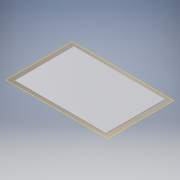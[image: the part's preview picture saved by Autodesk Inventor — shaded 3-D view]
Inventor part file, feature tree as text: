
AUTODESK INVENTOR PART (.ipt)
format: ipt  version: 2017 (Build 210142000, 142)  size: 94,720 bytes
history: native  units: mm
features: other x3, plane x1, extrude x1, sketch x1
ambient origin geometry x8: Origin, YZ Plane, XZ Plane, XY Plane, X Axis, Y Axis, Z Axis, Center Point
bodies: Solid1 (feature_tree)
feature tree (6):
  plane  "Work Plane1"
  extrude  "Extrusion1"  Depth=55.0mm
  sketch  "Sketch1"  dims[d3=85.0mm d4=55.0mm d5=0.3mm d6=0.0mm]
  parser-record x1  (decoder bookkeeping rows leaked as tree rows — omitted from the tree; the rows remain in map.json)
  other  "protoswitchboard.iam"
  other  "cover:1"
note: 1 file-system path scrubbed to <path> (originals preserved in map.json)
